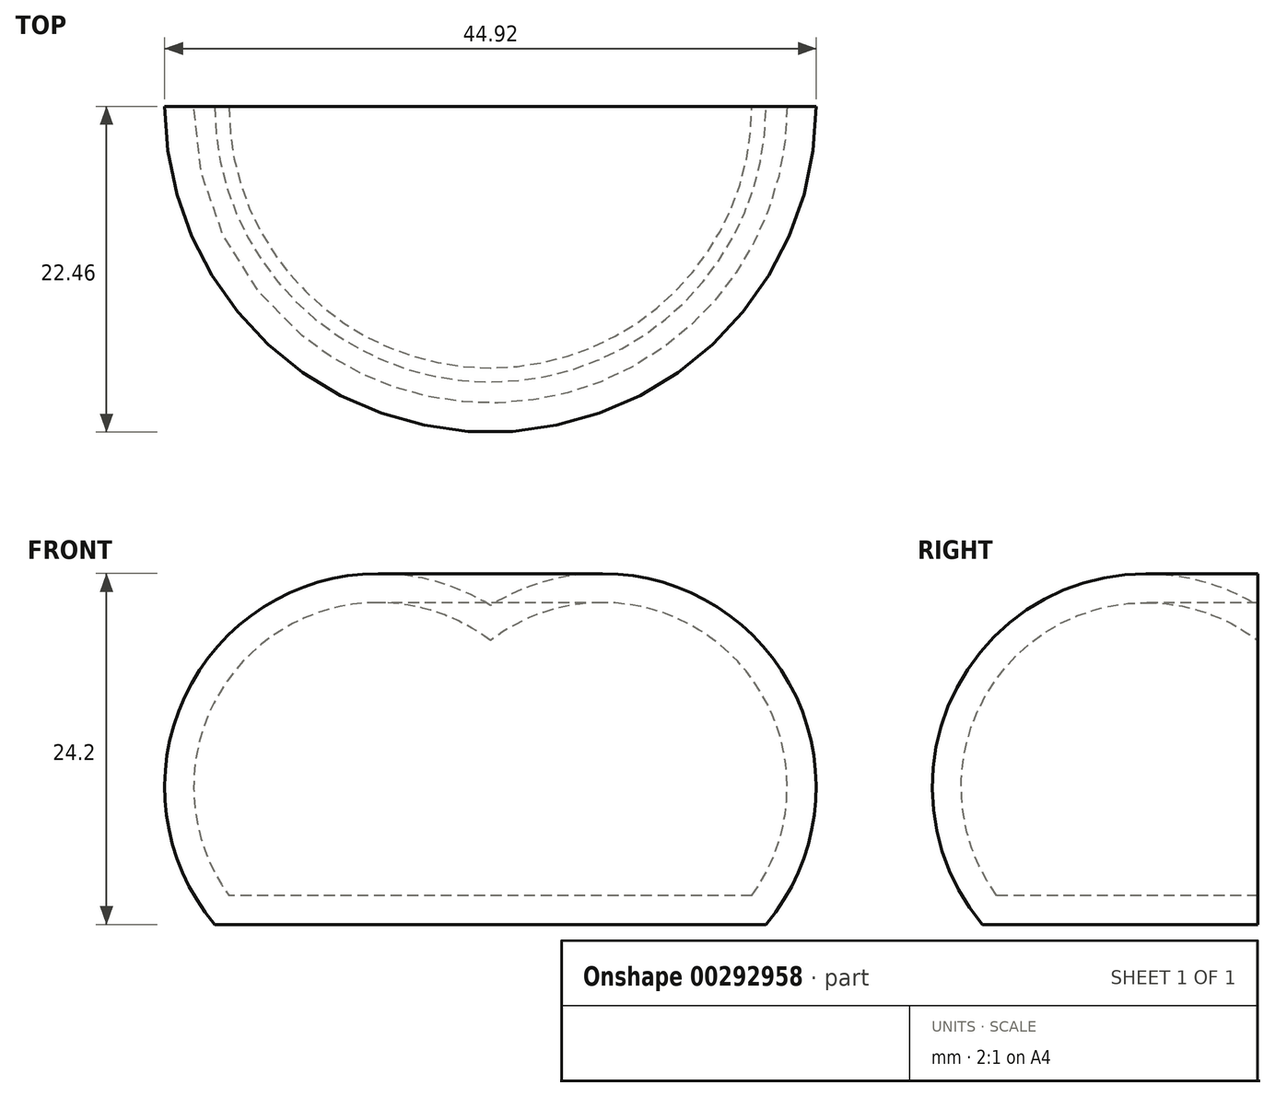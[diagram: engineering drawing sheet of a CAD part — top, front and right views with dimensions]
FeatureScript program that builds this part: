
annotation { "Feature Type Name" : "Feature", "Feature Type Description" : "" }
export const myFeature = defineFeature(function(context is Context, id is Id, definition is map)
    precondition{}
    {
        {
            var Q0;
            Q0=qCreatedBy(makeId("Front.planeOp"),FACE);
            var sketch = newSketch(context, id + "F0", { "sketchPlane" : qUnion([Q0])});
            skArc(sketch, "E0", {"start": v(0, 22) * mm, "mid": v(-18.88, 19.1) * mm, "end": v(-19, 0) * mm});
            skLineSegment(sketch, "E1", {"start": v(-19, 0) * mm, "end": v(0, 0) * mm});
            skLineSegment(sketch, "E2", {"start": v(0, 0) * mm, "end": v(0, 22) * mm});
            skSolve(sketch);
        }
        {
            var Q0;
            Q0 = qSketchRegion(id + "F0", true);
            var Q1;
            Q1=sQuery(id+"F0.wireOp",EDGE,"E2");
            revolve(context, id + "F1", {"entities" : qUnion([Q0]), "axis" : qUnion([Q1]), "revolveType" : RevolveType.ONE_DIRECTION, "angle" : 180 * degree});
        }
        {
            var Q0;
            Q0=makeQuery(id+"F1.opRevolve","CAP_FACE",FACE,{"disambiguationData":[OSD([sQuery(id+"F0.wireOp",EDGE,"E0"),sQuery(id+"F0.wireOp",EDGE,"E1"),sQuery(id+"F0.wireOp",EDGE,"E2")])],"isStart":false});
            var Q1;
            Q1=makeQuery(id+"F1.opRevolve","CAP_FACE",FACE,{"disambiguationData":[OSD([sQuery(id+"F0.wireOp",EDGE,"E0"),sQuery(id+"F0.wireOp",EDGE,"E1"),sQuery(id+"F0.wireOp",EDGE,"E2")])],"isStart":true});
            shell(context, id + "F2", {"entities" : qUnion([Q0, Q1]), "thickness" : 2 * mm});
        }
    });
